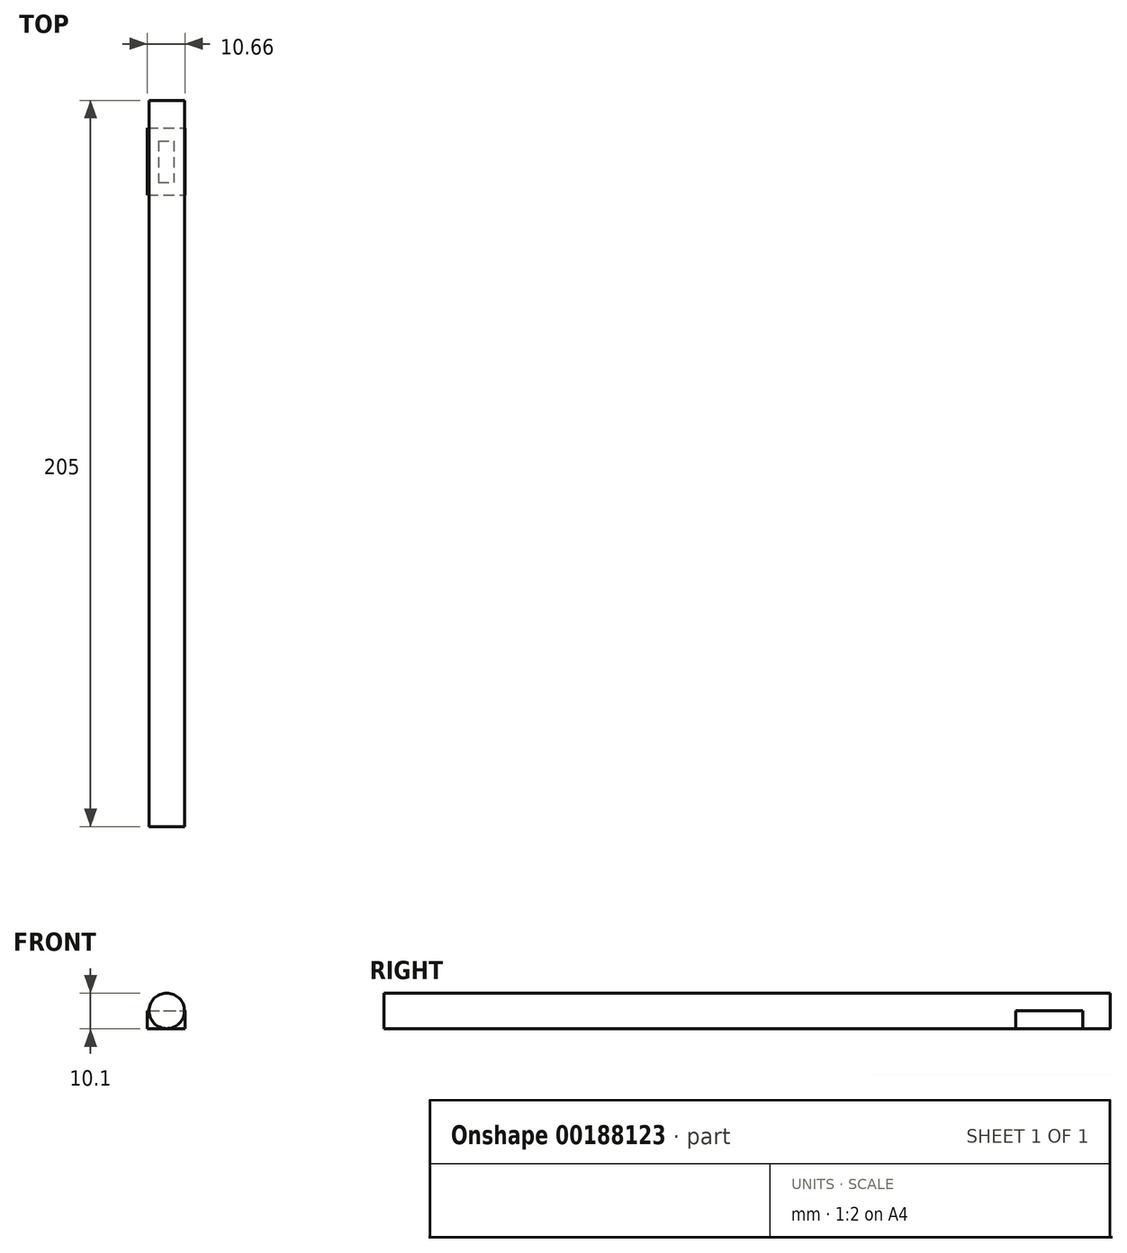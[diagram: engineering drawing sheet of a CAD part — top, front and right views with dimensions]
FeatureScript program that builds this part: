
annotation { "Feature Type Name" : "Feature", "Feature Type Description" : "" }
export const myFeature = defineFeature(function(context is Context, id is Id, definition is map)
    precondition{}
    {
        {
            var Q0;
            Q0=qCreatedBy(makeId("Front.planeOp"),FACE);
            var sketch = newSketch(context, id + "F4", { "sketchPlane" : qUnion([Q0])});
            skCircle(sketch, "E0", {"center": v(0, 0) * mm, "radius": 5 * mm});
            skSolve(sketch);
        }
        {
            var Q0;
            Q0 = qSketchRegion(id + "F4", true);
            extrude(context, id + "F0", {"entities" : qUnion([Q0]), "depth" : 205 * mm});
        }
        {
            var Q0;
            Q0=qCreatedBy(makeId("Top.planeOp"),FACE);
            var sketch = newSketch(context, id + "F1", { "sketchPlane" : qUnion([Q0])});
            skLineSegment(sketch, "E1.bottom", {"start": v(-5.49, -7.76) * mm, "end": v(5.17, -7.76) * mm});
            skLineSegment(sketch, "E1.top", {"start": v(-5.49, -26.71) * mm, "end": v(5.17, -26.71) * mm});
            skLineSegment(sketch, "E1.left", {"start": v(-5.49, -7.76) * mm, "end": v(-5.49, -26.71) * mm});
            skLineSegment(sketch, "E1.right", {"start": v(5.17, -7.76) * mm, "end": v(5.17, -26.71) * mm});
            skSolve(sketch);
        }
        {
            var Q0;
            Q0=makeQuery(id+"F1.imprint","IMPRINT",FACE,{"disambiguationData":[TD([[makeQuery(id+"F1.imprint","IMPRINT",EDGE,{"derivedFrom":sQuery(id+"F1.wireOp",EDGE,"E1.bottom")}),-1.0]])]});
            extrude(context, id + "F2", {"entities" : qUnion([Q0]), "oppositeDirection" : true, "depth" : 5 * mm});
        }
        {
            var Q0;
            Q0=makeQuery(id+"F2.opExtrude","CAP_FACE",FACE,{"disambiguationData":[OSD([sQuery(id+"F1.wireOp",EDGE,"E1.bottom"),sQuery(id+"F1.wireOp",EDGE,"E1.top"),sQuery(id+"F1.wireOp",EDGE,"E1.left"),sQuery(id+"F1.wireOp",EDGE,"E1.right")])],"isStart":false});
            var sketch = newSketch(context, id + "F3", { "sketchPlane" : qUnion([Q0])});
            skLineSegment(sketch, "E2.bottom", {"start": v(-2.37, 11.45) * mm, "end": v(2.05, 11.45) * mm});
            skLineSegment(sketch, "E2.top", {"start": v(-2.37, 23.15) * mm, "end": v(2.05, 23.15) * mm});
            skLineSegment(sketch, "E2.left", {"start": v(-2.37, 11.45) * mm, "end": v(-2.37, 23.15) * mm});
            skLineSegment(sketch, "E2.right", {"start": v(2.05, 11.45) * mm, "end": v(2.05, 23.15) * mm});
            skSolve(sketch);
        }
        {
            var Q0;
            Q0 = qSketchRegion(id + "F3", true);
            extrude(context, id + "F5", {"entities" : qUnion([Q0]), "depth" : 0.1 * mm});
        }
    });
